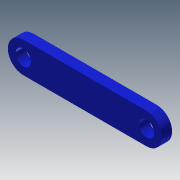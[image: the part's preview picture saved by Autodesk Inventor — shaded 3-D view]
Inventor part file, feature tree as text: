
AUTODESK INVENTOR PART (.ipt)
format: ipt  version: 2013 (Build 170138000, 138)  size: 94,720 bytes
history: native  units: mm
features: extrude x2, sketch x2
ambient origin geometry x8: Origin, YZ Plane, XZ Plane, XY Plane, X Axis, Y Axis, Z Axis, Center Point
bodies: Solid1 (feature_tree)
feature tree (4):
  extrude  "Extrusion1"  Depth=6.0mm
  extrude  "Extrusion2"  Depth=6.0mm
  sketch  "Sketch1"  dims[d0=24.0mm d1=6.0mm]
  sketch  "Sketch2"  dims[d2=6.0mm d3=6.0mm d4=2.0mm d5=0.0mm d6=2.0mm d7=3.0mm d8=3.0mm d9=2.0mm d10=0.0mm]
